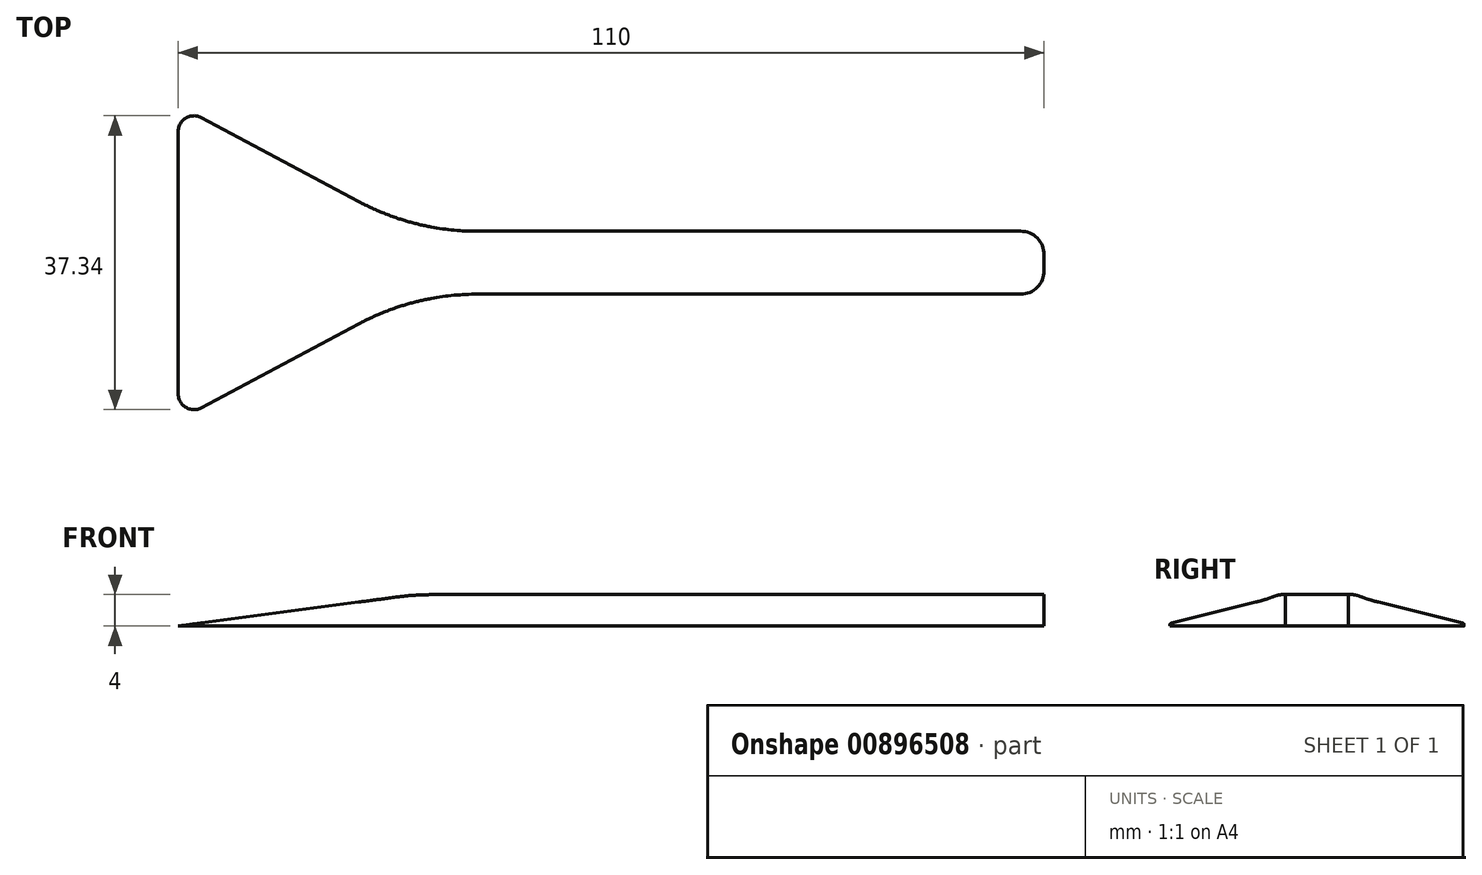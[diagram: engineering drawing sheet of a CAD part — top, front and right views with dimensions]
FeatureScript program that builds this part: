
annotation { "Feature Type Name" : "Feature", "Feature Type Description" : "" }
export const myFeature = defineFeature(function(context is Context, id is Id, definition is map)
    precondition{}
    {
        {
            var Q0;
            Q0=qCreatedBy(makeId("Top.planeOp"),FACE);
            var sketch = newSketch(context, id + "F0", { "sketchPlane" : qUnion([Q0])});
            skLineSegment(sketch, "E0.bottom", {"start": v(40, 4) * mm, "end": v(-40, 4) * mm});
            skLineSegment(sketch, "E0.top", {"start": v(40, -4) * mm, "end": v(-40, -4) * mm});
            skLineSegment(sketch, "E0.left", {"start": v(40, 4) * mm, "end": v(40, -4) * mm});
            skLineSegment(sketch, "E0.right", {"start": v(-40, 4) * mm, "end": v(-40, -4) * mm});
            skPoint(sketch, "E0.middle", {"position": v(0, 0) * mm});
            skLineSegment(sketch, "E1", {"start": v(-70, 0) * mm, "end": v(-40, 0) * mm, "construction": true});
            skLineSegment(sketch, "E2", {"start": v(-70, 20) * mm, "end": v(-70, -20) * mm});
            skLineSegment(sketch, "E3", {"start": v(-70, -20) * mm, "end": v(-40, -4) * mm});
            skLineSegment(sketch, "E4", {"start": v(-40, 4) * mm, "end": v(-70, 20) * mm});
            skSolve(sketch);
        }
        {
            var Q0;
            Q0=makeQuery(id+"F0.imprint","IMPRINT",FACE,{"disambiguationData":[TD([[makeQuery(id+"F0.imprint","IMPRINT",EDGE,{"derivedFrom":sQuery(id+"F0.wireOp",EDGE,"E0.bottom")}),1.0]])]});
            extrude(context, id + "F1", {"entities" : qUnion([Q0]), "depth" : 4 * mm, "offsetDistance" : 25 * mm});
        }
        {
            var Q0;
            Q0=makeQuery(id+"F1.opExtrude","SWEPT_EDGE",EDGE,{"disambiguationData":[OSD([sQuery(id+"F0.wireOp",EDGE,"E0.top"),sQuery(id+"F0.wireOp",EDGE,"E0.left")])]});
            var Q1;
            Q1=makeQuery(id+"F1.opExtrude","SWEPT_EDGE",EDGE,{"disambiguationData":[OSD([sQuery(id+"F0.wireOp",EDGE,"E0.bottom"),sQuery(id+"F0.wireOp",EDGE,"E0.left")])]});
            fillet(context, id + "F2", {"entities" : qUnion([Q0, Q1]), "tangentPropagation" : true, "radius" : 3 * mm, "defaultsChanged" : true, "vertexSettings" : [], "allowEdgeOverflow" : false});
        }
        {
            var Q0;
            Q0=makeQuery(id+"F0.imprint","IMPRINT",FACE,{"disambiguationData":[TD([[makeQuery(id+"F0.imprint","IMPRINT",EDGE,{"derivedFrom":sQuery(id+"F0.wireOp",EDGE,"E0.right")}),-1.0]])]});
            var Q1;
            Q1=makeQuery(id+"F1.opExtrude","SWEPT_FACE",FACE,{"disambiguationData":[OSD([sQuery(id+"F0.wireOp",EDGE,"E0.right")])]});
            var Q3;
            Q3=sQuery(id+"F0.wireOp",VERTEX,"E2.end");
            var Q4;
            Q4=makeQuery(id+"F1.opExtrude","CAP_VERTEX",VERTEX,{"disambiguationData":[OSD([sQuery(id+"F0.wireOp",EDGE,"E0.top"),sQuery(id+"F0.wireOp",EDGE,"E0.right"),sQuery(id+"F0.wireOp",EDGE,"E3")])],"isStart":false});
            loft(context, id + "F3", {"operationType" : NewBodyOperationType.ADD, "sheetProfilesArray" : [{ "sheetProfileEntities" : qUnion([Q0]) }, { "sheetProfileEntities" : qUnion([Q1]) }], "matchConnections" : true, "connections" : [{ "connectionEntities" : qUnion([Q3, Q4]), "connectionEdgeQueries" : qUnion([]), "connectionEdgeParameters" : [] }]});
        }
        {
            var Q0;
            {var subQ0=sQuery(id+"F0.wireOp",EDGE,"E3");var subQ1=sQuery(id+"F0.wireOp",EDGE,"E0.right");var subQ2=sQuery(id+"F0.wireOp",EDGE,"E0.top");Q0=makeQuery(id+"F3.boolean.opBoolean","MERGE",EDGE,{"derivedFrom":[makeQuery(id+"F1.opExtrude","SWEPT_EDGE",EDGE,{"disambiguationData":[OSD([subQ2,subQ1,subQ0])]}),makeQuery(id+"F3.opLoft","MID_CAP_EDGE",EDGE,{"disambiguationData":[OSD([subQ2,subQ1,subQ0])],"capPos":1.0})]});}
            var Q1;
            {var subQ0=sQuery(id+"F0.wireOp",EDGE,"E4");var subQ1=sQuery(id+"F0.wireOp",EDGE,"E0.right");var subQ2=sQuery(id+"F0.wireOp",EDGE,"E0.bottom");Q1=makeQuery(id+"F3.boolean.opBoolean","MERGE",EDGE,{"derivedFrom":[makeQuery(id+"F1.opExtrude","SWEPT_EDGE",EDGE,{"disambiguationData":[OSD([subQ2,subQ1,subQ0])]}),makeQuery(id+"F3.opLoft","MID_CAP_EDGE",EDGE,{"disambiguationData":[OSD([subQ2,subQ1,subQ0])],"capPos":1.0})]});}
            var Q2;
            {var subQ0=sQuery(id+"F0.wireOp",EDGE,"E0.right");Q2=makeQuery(id+"F3.boolean.opBoolean","MERGE",EDGE,{"derivedFrom":[makeQuery(id+"F1.opExtrude","CAP_EDGE",EDGE,{"disambiguationData":[OSD([subQ0])],"isStart":false}),makeQuery(id+"F3.opLoft","MID_CAP_EDGE",EDGE,{"disambiguationData":[OSD([sQuery(id+"F0.wireOp",EDGE,"E0.bottom"),sQuery(id+"F0.wireOp",EDGE,"E0.top"),subQ0,sQuery(id+"F0.wireOp",EDGE,"E3"),sQuery(id+"F0.wireOp",EDGE,"E4")])],"capPos":1.0})]});}
            fillet(context, id + "F4", {"entities" : qUnion([Q0, Q1, Q2]), "tangentPropagation" : true, "radius" : 32 * mm, "defaultsChanged" : false, "vertexSettings" : [], "allowEdgeOverflow" : false});
        }
        {
            var Q0;
            Q0=makeQuery(id+"F0.imprint","IMPRINT",FACE,{"disambiguationData":[TD([[makeQuery(id+"F0.imprint","IMPRINT",EDGE,{"derivedFrom":sQuery(id+"F0.wireOp",EDGE,"E0.right")}),-1.0]])]});
            var sketch = newSketch(context, id + "F5", { "sketchPlane" : qUnion([Q0])});
            skLineSegment(sketch, "E5.0", {"start": v(-67.06, -18.43) * mm, "end": v(-40, -4) * mm});
            skLineSegment(sketch, "E6.0", {"start": v(-70, 16.67) * mm, "end": v(-70, -16.67) * mm});
            skLineSegment(sketch, "E7.0", {"start": v(-40, 4) * mm, "end": v(-67.06, 18.43) * mm});
            skPoint(sketch, "E8.visualSharp", {"position": v(-70, -20) * mm});
            skArc(sketch, "E8.filletArc", {"start": v(-70, -16.67) * mm, "mid": v(-69.03, -18.38) * mm, "end": v(-67.06, -18.43) * mm});
            skPoint(sketch, "E9.visualSharp", {"position": v(-70, 20) * mm});
            skArc(sketch, "E9.filletArc", {"start": v(-67.06, 18.43) * mm, "mid": v(-69.03, 18.38) * mm, "end": v(-70, 16.67) * mm});
            skLineSegment(sketch, "E10", {"start": v(-70, -20) * mm, "end": v(-67.06, -18.43) * mm});
            skLineSegment(sketch, "E11", {"start": v(-70, -20) * mm, "end": v(-70, -16.67) * mm});
            skLineSegment(sketch, "E12", {"start": v(-70, 16.67) * mm, "end": v(-70, 20) * mm});
            skLineSegment(sketch, "E13", {"start": v(-67.06, 18.43) * mm, "end": v(-70, 20) * mm});
            skSolve(sketch);
        }
        {
            var Q0;
            Q0 = qSketchRegion(id + "F5", true);
            extrude(context, id + "F6", {"entities" : qUnion([Q0]), "operationType" : NewBodyOperationType.REMOVE, "endBound" : BoundingType.THROUGH_ALL, "depth" : 25 * mm, "offsetDistance" : 25 * mm});
        }
    });
